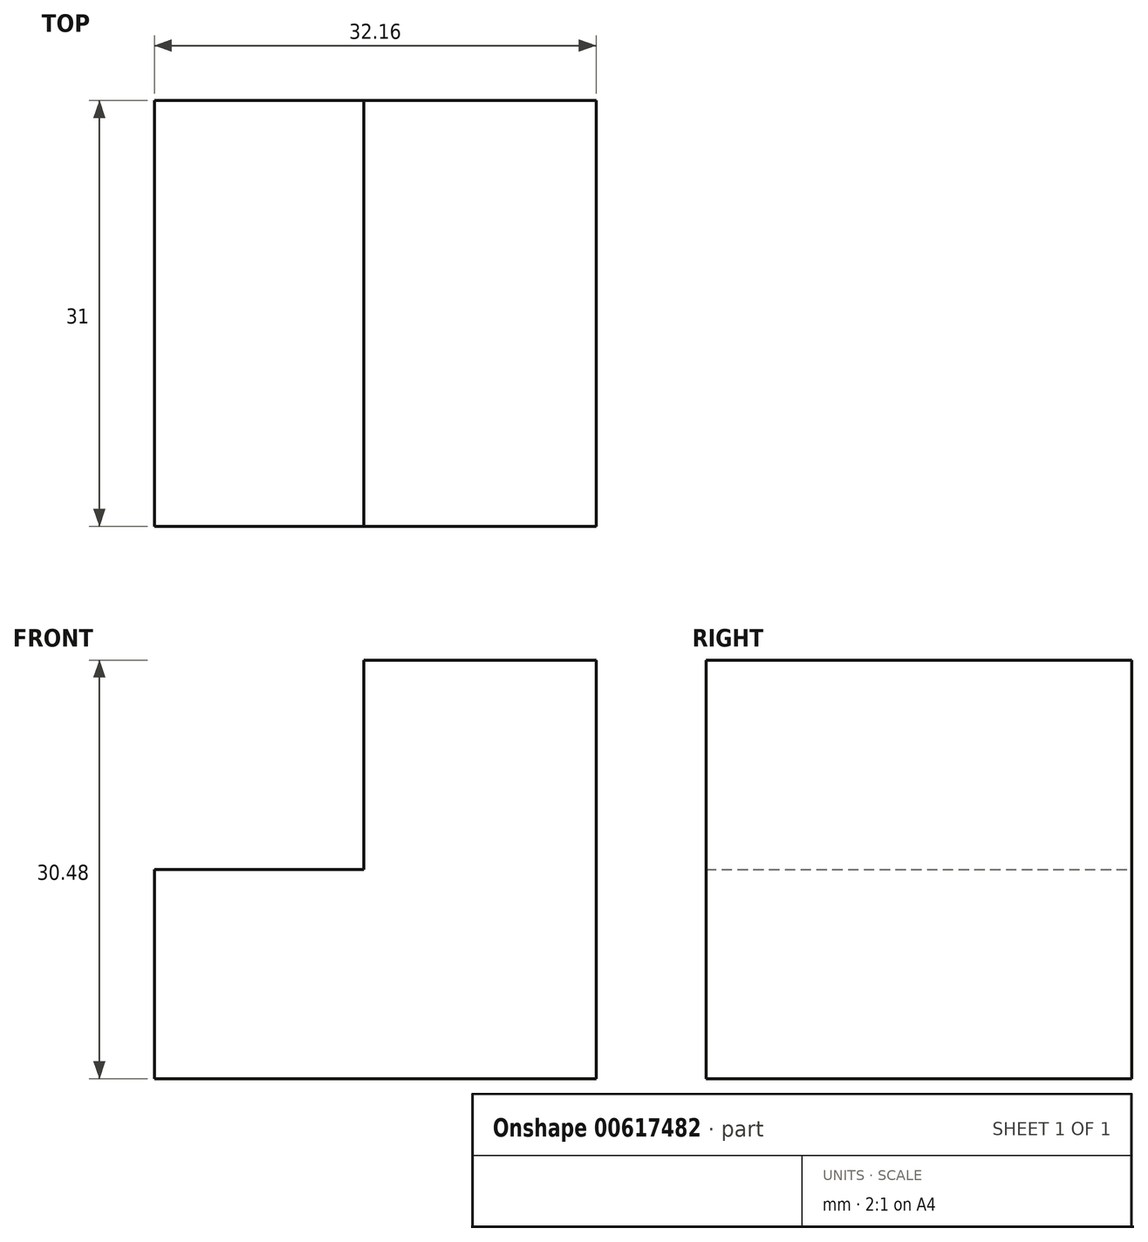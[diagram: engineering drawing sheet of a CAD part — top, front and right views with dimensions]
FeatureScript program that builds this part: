
annotation { "Feature Type Name" : "Feature", "Feature Type Description" : "" }
export const myFeature = defineFeature(function(context is Context, id is Id, definition is map)
    precondition{}
    {
        {
            var Q0;
            Q0=qCreatedBy(makeId("Front.planeOp"),FACE);
            var sketch = newSketch(context, id + "F0", { "sketchPlane" : qUnion([Q0])});
            skLineSegment(sketch, "E0", {"start": v(0, 0) * mm, "end": v(0, 15.24) * mm});
            skLineSegment(sketch, "E1", {"start": v(0, 15.24) * mm, "end": v(0, 30.48) * mm});
            skLineSegment(sketch, "E2", {"start": v(0, 30.48) * mm, "end": v(-16.92, 30.48) * mm});
            skLineSegment(sketch, "E3", {"start": v(-16.92, 30.48) * mm, "end": v(-16.92, 15.24) * mm});
            skLineSegment(sketch, "E4", {"start": v(-16.92, 15.24) * mm, "end": v(-32.16, 15.24) * mm});
            skLineSegment(sketch, "E5", {"start": v(-32.16, 15.24) * mm, "end": v(-32.16, 0) * mm});
            skLineSegment(sketch, "E6", {"start": v(-32.16, 0) * mm, "end": v(0, 0) * mm});
            skSolve(sketch);
        }
        {
            var Q0;
            Q0 = qSketchRegion(id + "F0", true);
            extrude(context, id + "F1", {"entities" : qUnion([Q0]), "depth" : 31 * mm, "offsetDistance" : 25.4 * mm});
        }
    });
